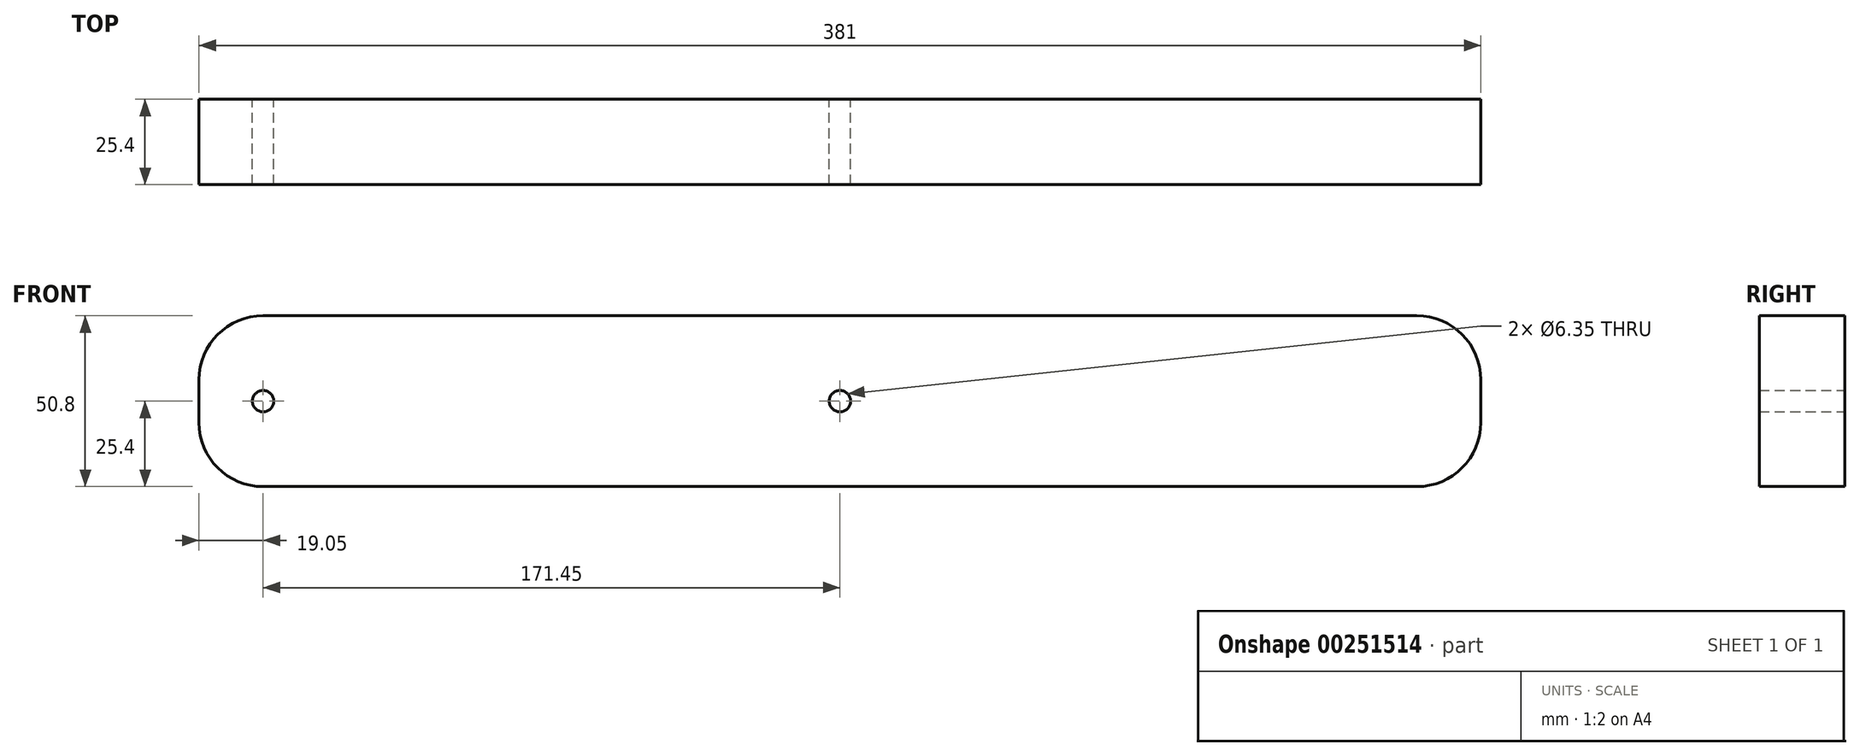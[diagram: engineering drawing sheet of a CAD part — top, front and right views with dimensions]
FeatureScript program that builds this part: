
annotation { "Feature Type Name" : "Feature", "Feature Type Description" : "" }
export const myFeature = defineFeature(function(context is Context, id is Id, definition is map)
    precondition{}
    {
        {
            var Q0;
            Q0=qCreatedBy(makeId("Front.planeOp"),FACE);
            var sketch = newSketch(context, id + "F0", { "sketchPlane" : qUnion([Q0])});
            skLineSegment(sketch, "E0", {"start": v(0, 19.05) * mm, "end": v(0, 31.75) * mm});
            skLineSegment(sketch, "E1", {"start": v(19.05, 50.8) * mm, "end": v(361.95, 50.8) * mm});
            skLineSegment(sketch, "E2", {"start": v(381, 31.75) * mm, "end": v(381, 19.05) * mm});
            skLineSegment(sketch, "E3", {"start": v(361.95, 0) * mm, "end": v(19.05, 0) * mm});
            skPoint(sketch, "E4.visualSharp", {"position": v(0, 50.8) * mm});
            skArc(sketch, "E4.filletArc", {"start": v(19.05, 50.8) * mm, "mid": v(5.58, 45.22) * mm, "end": v(0, 31.75) * mm});
            skPoint(sketch, "E5.visualSharp", {"position": v(0, 0) * mm});
            skArc(sketch, "E5.filletArc", {"start": v(0, 19.05) * mm, "mid": v(5.58, 5.58) * mm, "end": v(19.05, 0) * mm});
            skPoint(sketch, "E6.visualSharp", {"position": v(381, 50.8) * mm});
            skArc(sketch, "E6.filletArc", {"start": v(381, 31.75) * mm, "mid": v(375.42, 45.22) * mm, "end": v(361.95, 50.8) * mm});
            skPoint(sketch, "E7.visualSharp", {"position": v(381, 0) * mm});
            skArc(sketch, "E7.filletArc", {"start": v(361.95, 0) * mm, "mid": v(375.42, 5.58) * mm, "end": v(381, 19.05) * mm});
            skPoint(sketch, "E8.centerSnap0", {"position": v(381, 25.4) * mm});
            skCircle(sketch, "E9", {"center": v(19.05, 25.4) * mm, "radius": 3.18 * mm});
            skPoint(sketch, "E9.centerSnap0", {"position": v(0, 25.4) * mm});
            skPoint(sketch, "E10", {"position": v(190.5, 50.8) * mm});
            skCircle(sketch, "E11", {"center": v(190.5, 25.4) * mm, "radius": 3.18 * mm});
            skSolve(sketch);
        }
        {
            var Q0;
            Q0=makeQuery(id+"F0.imprint","IMPRINT",FACE,{"disambiguationData":[TD([[makeQuery(id+"F0.imprint","IMPRINT",EDGE,{"derivedFrom":sQuery(id+"F0.wireOp",EDGE,"E0")}),-1.0]])]});
            extrude(context, id + "F1", {"entities" : qUnion([Q0]), "depth" : 25.4 * mm});
        }
    });
